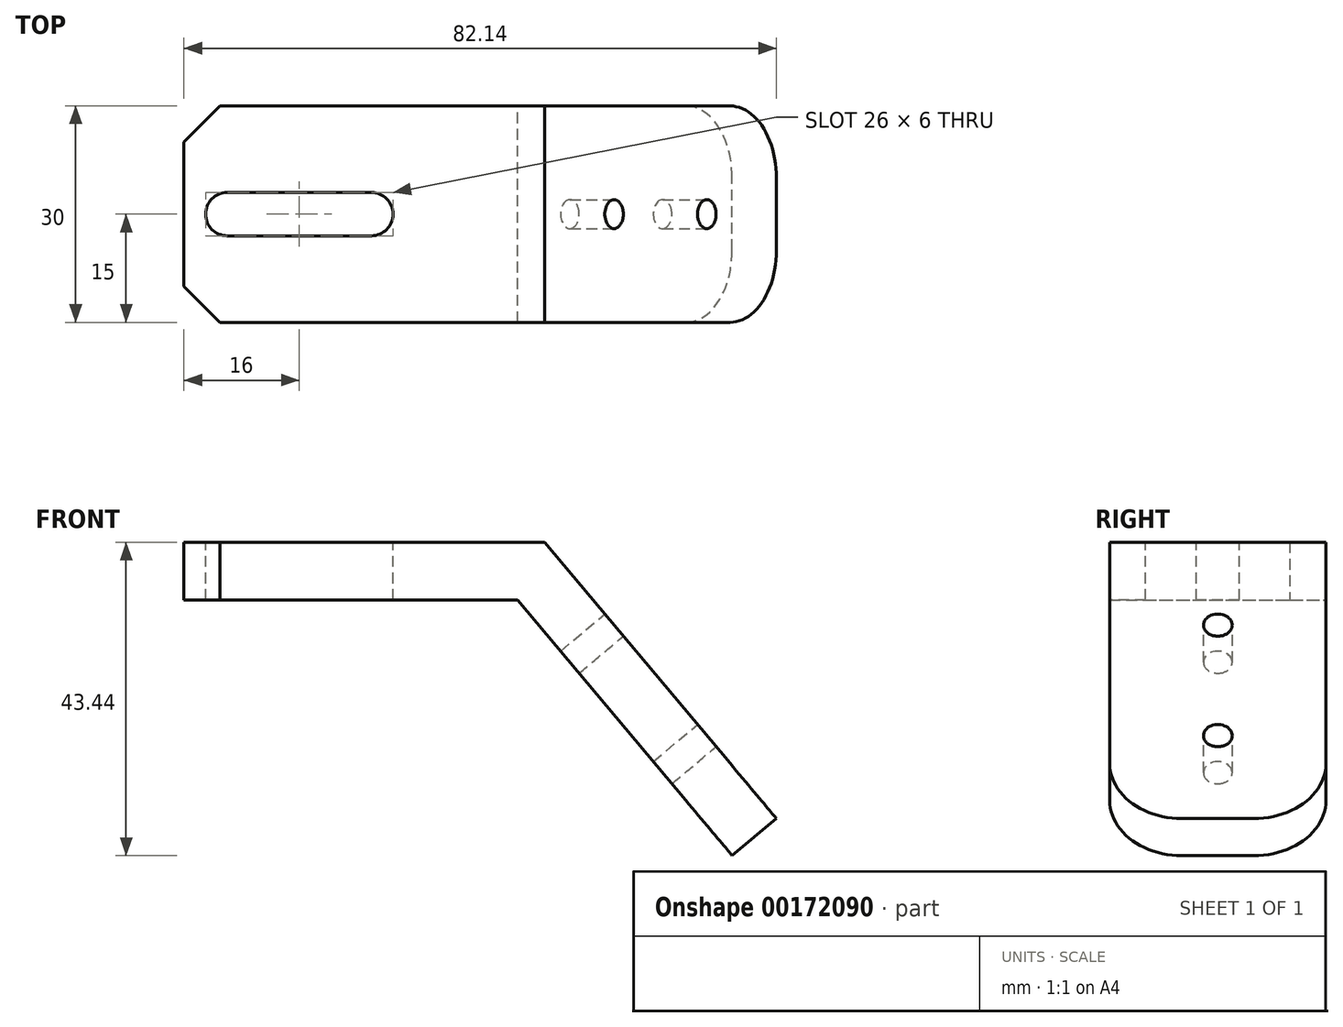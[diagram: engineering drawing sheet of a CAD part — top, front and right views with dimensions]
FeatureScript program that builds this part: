
annotation { "Feature Type Name" : "Feature", "Feature Type Description" : "" }
export const myFeature = defineFeature(function(context is Context, id is Id, definition is map)
    precondition{}
    {
        {
            var Q0;
            Q0=qCreatedBy(makeId("Front.planeOp"),FACE);
            var sketch = newSketch(context, id + "F0", { "sketchPlane" : qUnion([Q0])});
            skLineSegment(sketch, "E0", {"start": v(0, 0) * mm, "end": v(46.27, 0) * mm});
            skLineSegment(sketch, "E1", {"start": v(46.27, 0) * mm, "end": v(76.01, -35.44) * mm});
            skLineSegment(sketch, "E2.0", {"start": v(50, 8) * mm, "end": v(82.14, -30.3) * mm});
            skLineSegment(sketch, "E2.1", {"start": v(0, 8) * mm, "end": v(50, 8) * mm});
            skLineSegment(sketch, "E3", {"start": v(76.01, -35.44) * mm, "end": v(82.14, -30.3) * mm});
            skLineSegment(sketch, "E4", {"start": v(0, 0) * mm, "end": v(0, 8) * mm});
            skSolve(sketch);
        }
        {
            var Q0;
            Q0 = qSketchRegion(id + "F0", true);
            extrude(context, id + "F1", {"entities" : qUnion([Q0]), "endBound" : BoundingType.SYMMETRIC, "depth" : 30 * mm});
        }
        {
            var Q0;
            Q0=makeQuery(id+"F1.opExtrude","SWEPT_FACE",FACE,{"disambiguationData":[OSD([sQuery(id+"F0.wireOp",EDGE,"E2.1")])]});
            var sketch = newSketch(context, id + "F2", { "sketchPlane" : qUnion([Q0])});
            skLineSegment(sketch, "E5", {"start": v(6, 0) * mm, "end": v(26, 0) * mm});
            skArc(sketch, "E6.0.startCap", {"start": v(6, -3) * mm, "mid": v(3, 0) * mm, "end": v(6, 3) * mm});
            skArc(sketch, "E6.0.endCap", {"start": v(26, 3) * mm, "mid": v(29, 0) * mm, "end": v(26, -3) * mm});
            skLineSegment(sketch, "E6.0.left", {"start": v(6, 3) * mm, "end": v(26, 3) * mm});
            skLineSegment(sketch, "E6.0.right", {"start": v(6, -3) * mm, "end": v(26, -3) * mm});
            skSolve(sketch);
        }
        {
            var Q0;
            Q0 = qSketchRegion(id + "F2", true);
            extrude(context, id + "F3", {"entities" : qUnion([Q0]), "operationType" : NewBodyOperationType.REMOVE, "endBound" : BoundingType.THROUGH_ALL, "oppositeDirection" : true, "depth" : 25 * mm});
        }
        {
            var Q0;
            Q0=makeQuery(id+"F1.opExtrude","SWEPT_FACE",FACE,{"disambiguationData":[OSD([sQuery(id+"F0.wireOp",EDGE,"E2.0")])]});
            var sketch = newSketch(context, id + "F4", { "sketchPlane" : qUnion([Q0])});
            skPoint(sketch, "E7", {"position": v(0, -41.01) * mm});
            skPoint(sketch, "E8", {"position": v(0, -61.01) * mm});
            skSolve(sketch);
        }
        {
            var Q0;
            Q0=sQuery(id+"F4.wireOp",VERTEX,"E7");
            var Q1;
            Q1=sQuery(id+"F4.wireOp",VERTEX,"E8");
            var Q2;
            Q2=makeQuery(id+"F1.opExtrude","SWEPT_BODY",BODY,{"disambiguationData":[OSD([sQuery(id+"F0.wireOp",EDGE,"E0"),sQuery(id+"F0.wireOp",EDGE,"E1"),sQuery(id+"F0.wireOp",EDGE,"E2.0"),sQuery(id+"F0.wireOp",EDGE,"E2.1"),sQuery(id+"F0.wireOp",EDGE,"E3"),sQuery(id+"F0.wireOp",EDGE,"E4")])]});
            hole(context, id + "F5", {"style" : HoleStyle.SIMPLE, "endStyle" : HoleEndStyle.THROUGH, "holeDiameter" : 4 * mm, "locations" : qUnion([Q0, Q1]), "scope" : qUnion([Q2]), "isTappedThrough" : true});
        }
        {
            var Q0;
            Q0=makeQuery(id+"F1.opExtrude","CAP_EDGE",EDGE,{"disambiguationData":[OSD([sQuery(id+"F0.wireOp",EDGE,"E3")])],"isStart":false});
            var Q1;
            Q1=makeQuery(id+"F1.opExtrude","CAP_EDGE",EDGE,{"disambiguationData":[OSD([sQuery(id+"F0.wireOp",EDGE,"E3")])],"isStart":true});
            fillet(context, id + "F6", {"entities" : qUnion([Q0, Q1]), "radius" : 10 * mm, "tangentPropagation" : true, "allowEdgeOverflow" : false});
        }
        {
            var Q0;
            Q0=makeQuery(id+"F1.opExtrude","CAP_EDGE",EDGE,{"disambiguationData":[OSD([sQuery(id+"F0.wireOp",EDGE,"E4")])],"isStart":false});
            var Q1;
            Q1=makeQuery(id+"F1.opExtrude","CAP_EDGE",EDGE,{"disambiguationData":[OSD([sQuery(id+"F0.wireOp",EDGE,"E4")])],"isStart":true});
            chamfer(context, id + "F7", {"entities" : qUnion([Q0, Q1]), "width" : 5 * mm, "tangentPropagation" : true});
        }
    });
